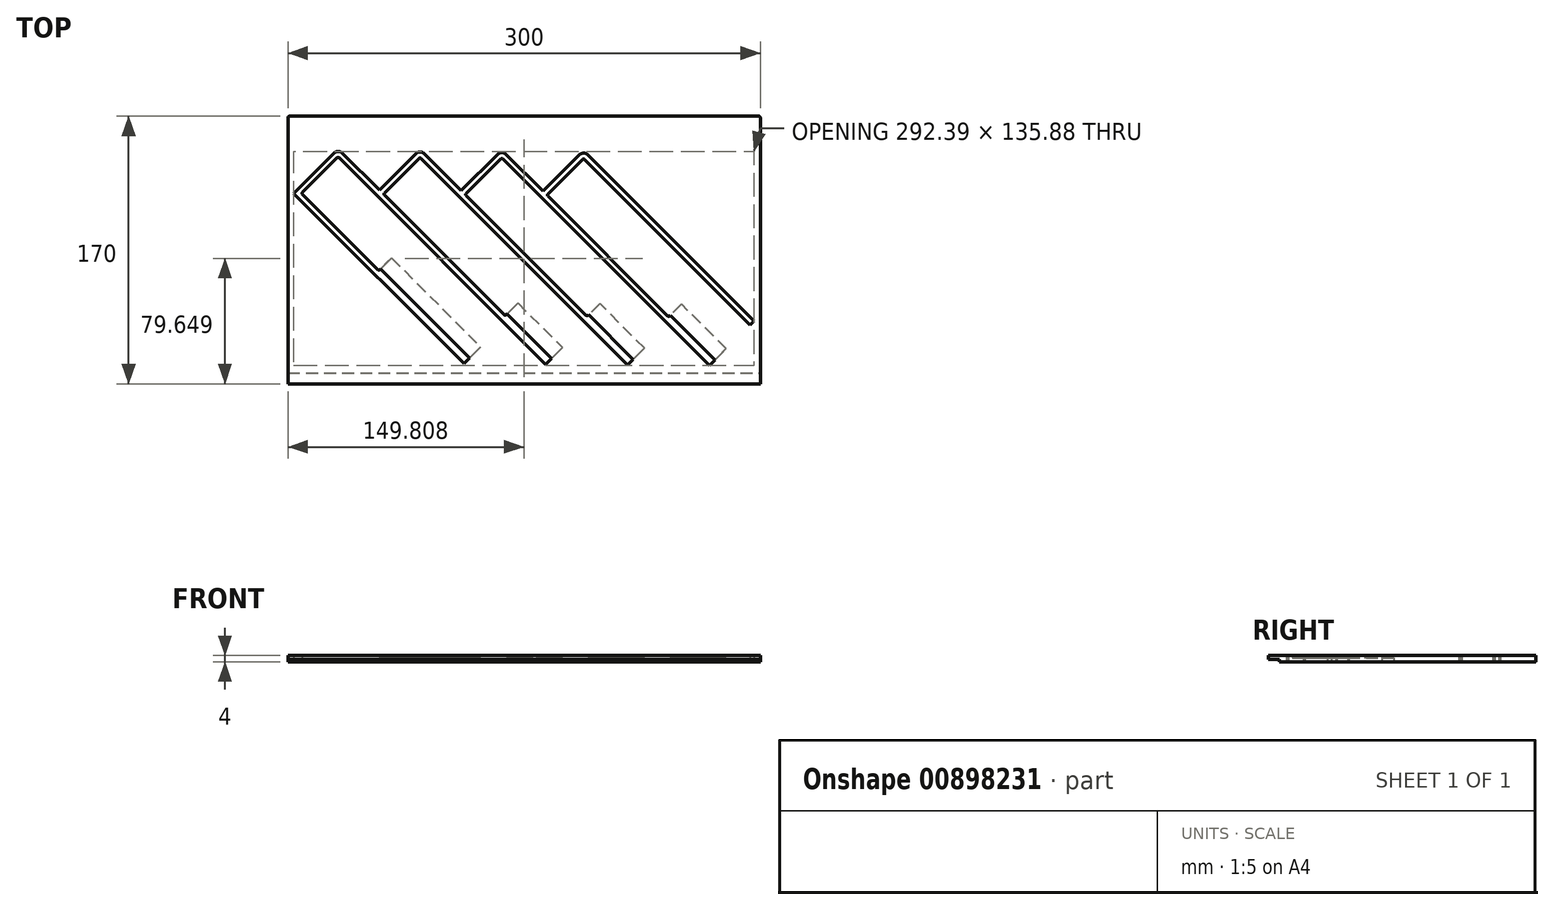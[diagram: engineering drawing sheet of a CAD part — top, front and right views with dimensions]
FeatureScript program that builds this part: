
annotation { "Feature Type Name" : "Feature", "Feature Type Description" : "" }
export const myFeature = defineFeature(function(context is Context, id is Id, definition is map)
    precondition{}
    {
        {
            var Q0;
            Q0=qCreatedBy(makeId("Top.planeOp"),FACE);
            var sketch = newSketch(context, id + "F0", { "sketchPlane" : qUnion([Q0])});
            skLineSegment(sketch, "E0.left", {"start": v(295.71, -89.91) * mm, "end": v(295.71, 79.09) * mm});
            skPoint(sketch, "E0.middle", {"position": v(0, 0) * mm});
            skLineSegment(sketch, "E1", {"start": v(186.35, 55.44) * mm, "end": v(291.71, -49.91) * mm});
            skLineSegment(sketch, "E2", {"start": v(291.71, -49.91) * mm, "end": v(289.24, -52.39) * mm});
            skLineSegment(sketch, "E3", {"start": v(263.43, -78.2) * mm, "end": v(155.24, 29.99) * mm});
            skLineSegment(sketch, "E4", {"start": v(157.72, 32.46) * mm, "end": v(180.7, 55.44) * mm});
            skLineSegment(sketch, "E5", {"start": v(236.91, -46.73) * mm, "end": v(160.9, 29.28) * mm});
            skLineSegment(sketch, "E6", {"start": v(160.9, 30.7) * mm, "end": v(182.82, 52.62) * mm});
            skLineSegment(sketch, "E7", {"start": v(184.23, 52.62) * mm, "end": v(289.24, -52.39) * mm});
            skLineSegment(sketch, "E8.trimOffspring", {"start": v(265.9, -75.72) * mm, "end": v(263.43, -78.2) * mm});
            skLineSegment(sketch, "E9", {"start": v(134.38, 55.8) * mm, "end": v(157.72, 32.46) * mm});
            skLineSegment(sketch, "E10", {"start": v(211.46, -77.84) * mm, "end": v(103.27, 30.34) * mm});
            skLineSegment(sketch, "E11", {"start": v(105.74, 32.82) * mm, "end": v(128.72, 55.8) * mm});
            skLineSegment(sketch, "E12", {"start": v(184.94, -46.38) * mm, "end": v(108.93, 29.64) * mm});
            skLineSegment(sketch, "E13", {"start": v(108.93, 31.05) * mm, "end": v(130.85, 52.97) * mm});
            skLineSegment(sketch, "E14", {"start": v(132.26, 52.97) * mm, "end": v(155.24, 29.99) * mm});
            skLineSegment(sketch, "E15.trimOffspring", {"start": v(213.93, -75.37) * mm, "end": v(211.46, -77.84) * mm});
            skLineSegment(sketch, "E16", {"start": v(82.4, 56.15) * mm, "end": v(105.74, 32.82) * mm});
            skLineSegment(sketch, "E17", {"start": v(159.48, -77.5) * mm, "end": v(51.3, 30.7) * mm});
            skLineSegment(sketch, "E18", {"start": v(53.77, 33.17) * mm, "end": v(76.75, 56.15) * mm});
            skLineSegment(sketch, "E19", {"start": v(132.97, -46.03) * mm, "end": v(56.95, 29.99) * mm});
            skLineSegment(sketch, "E20", {"start": v(56.95, 31.4) * mm, "end": v(78.87, 53.32) * mm});
            skLineSegment(sketch, "E21", {"start": v(80.29, 53.32) * mm, "end": v(103.27, 30.34) * mm});
            skLineSegment(sketch, "E22.trimOffspring", {"start": v(161.96, -75.02) * mm, "end": v(159.48, -77.5) * mm});
            skLineSegment(sketch, "E23", {"start": v(30.44, 56.5) * mm, "end": v(53.77, 33.17) * mm});
            skLineSegment(sketch, "E24", {"start": v(107.51, -77.14) * mm, "end": v(-0.68, 31.05) * mm});
            skLineSegment(sketch, "E25", {"start": v(-0.68, 31.05) * mm, "end": v(24.78, 56.5) * mm});
            skLineSegment(sketch, "E26", {"start": v(52.71, -17.39) * mm, "end": v(4.98, 30.34) * mm});
            skLineSegment(sketch, "E27", {"start": v(4.98, 31.76) * mm, "end": v(26.9, 53.68) * mm});
            skLineSegment(sketch, "E28", {"start": v(28.32, 53.68) * mm, "end": v(51.3, 30.7) * mm});
            skLineSegment(sketch, "E29.trimOffspring", {"start": v(109.99, -74.66) * mm, "end": v(107.51, -77.14) * mm});
            skLineSegment(sketch, "E30", {"start": v(-4.29, -89.91) * mm, "end": v(295.71, -89.91) * mm});
            skLineSegment(sketch, "E31", {"start": v(265.9, -75.72) * mm, "end": v(266.96, -74.66) * mm});
            skLineSegment(sketch, "E32", {"start": v(266.96, -74.66) * mm, "end": v(238.68, -46.38) * mm});
            skLineSegment(sketch, "E33", {"start": v(238.68, -46.38) * mm, "end": v(238.33, -46.73) * mm});
            skLineSegment(sketch, "E34", {"start": v(213.93, -75.37) * mm, "end": v(215, -74.3) * mm});
            skLineSegment(sketch, "E35", {"start": v(215, -74.3) * mm, "end": v(186.7, -46.03) * mm});
            skLineSegment(sketch, "E36", {"start": v(186.7, -46.03) * mm, "end": v(186.35, -46.38) * mm});
            skLineSegment(sketch, "E37", {"start": v(161.96, -75.02) * mm, "end": v(163.02, -73.96) * mm});
            skLineSegment(sketch, "E38", {"start": v(163.02, -73.96) * mm, "end": v(134.73, -45.67) * mm});
            skLineSegment(sketch, "E39", {"start": v(134.73, -45.67) * mm, "end": v(134.38, -46.03) * mm});
            skLineSegment(sketch, "E40", {"start": v(109.99, -74.66) * mm, "end": v(111.05, -73.6) * mm});
            skLineSegment(sketch, "E41", {"start": v(111.05, -73.6) * mm, "end": v(54.48, -17.03) * mm});
            skLineSegment(sketch, "E42", {"start": v(54.48, -17.03) * mm, "end": v(54.12, -17.39) * mm});
            skPoint(sketch, "E43.visualSharp", {"position": v(27.6, 59.33) * mm});
            skArc(sketch, "E43.filletArc", {"start": v(30.44, 56.5) * mm, "mid": v(27.6, 57.68) * mm, "end": v(24.78, 56.5) * mm});
            skPoint(sketch, "E44.visualSharp", {"position": v(79.58, 58.98) * mm});
            skArc(sketch, "E44.filletArc", {"start": v(82.4, 56.15) * mm, "mid": v(79.58, 57.32) * mm, "end": v(76.75, 56.15) * mm});
            skPoint(sketch, "E45.visualSharp", {"position": v(131.55, 58.63) * mm});
            skArc(sketch, "E45.filletArc", {"start": v(134.38, 55.8) * mm, "mid": v(131.55, 56.97) * mm, "end": v(128.72, 55.8) * mm});
            skPoint(sketch, "E46.visualSharp", {"position": v(183.53, 58.27) * mm});
            skArc(sketch, "E46.filletArc", {"start": v(186.35, 55.44) * mm, "mid": v(183.53, 56.62) * mm, "end": v(180.7, 55.44) * mm});
            skLineSegment(sketch, "E47", {"start": v(-4.29, 79.09) * mm, "end": v(-4.29, -89.91) * mm});
            skPoint(sketch, "E48.visualSharp", {"position": v(4.27, 31.05) * mm});
            skArc(sketch, "E48.filletArc", {"start": v(4.98, 31.76) * mm, "mid": v(4.69, 31.05) * mm, "end": v(4.98, 30.34) * mm});
            skPoint(sketch, "E49.visualSharp", {"position": v(56.25, 30.7) * mm});
            skArc(sketch, "E49.filletArc", {"start": v(56.95, 31.4) * mm, "mid": v(56.66, 30.7) * mm, "end": v(56.95, 29.99) * mm});
            skPoint(sketch, "E50.visualSharp", {"position": v(108.22, 30.34) * mm});
            skArc(sketch, "E50.filletArc", {"start": v(108.93, 31.05) * mm, "mid": v(108.63, 30.34) * mm, "end": v(108.93, 29.64) * mm});
            skPoint(sketch, "E51.visualSharp", {"position": v(160.2, 29.99) * mm});
            skArc(sketch, "E51.filletArc", {"start": v(160.9, 30.7) * mm, "mid": v(160.6, 29.99) * mm, "end": v(160.9, 29.28) * mm});
            skPoint(sketch, "E52.visualSharp", {"position": v(27.6, 54.38) * mm});
            skArc(sketch, "E52.filletArc", {"start": v(28.32, 53.68) * mm, "mid": v(27.6, 53.97) * mm, "end": v(26.9, 53.68) * mm});
            skPoint(sketch, "E53.visualSharp", {"position": v(79.58, 54.03) * mm});
            skArc(sketch, "E53.filletArc", {"start": v(80.29, 53.32) * mm, "mid": v(79.58, 53.62) * mm, "end": v(78.87, 53.32) * mm});
            skPoint(sketch, "E54.visualSharp", {"position": v(131.55, 53.68) * mm});
            skArc(sketch, "E54.filletArc", {"start": v(132.26, 52.97) * mm, "mid": v(131.55, 53.26) * mm, "end": v(130.85, 52.97) * mm});
            skPoint(sketch, "E55.visualSharp", {"position": v(183.53, 53.32) * mm});
            skArc(sketch, "E55.filletArc", {"start": v(184.23, 52.62) * mm, "mid": v(183.53, 52.9) * mm, "end": v(182.82, 52.62) * mm});
            skLineSegment(sketch, "E56", {"start": v(-3.29, 80.09) * mm, "end": v(294.71, 80.09) * mm});
            skPoint(sketch, "E57.visualSharp", {"position": v(-4.29, 80.09) * mm});
            skArc(sketch, "E57.filletArc", {"start": v(-3.29, 80.09) * mm, "mid": v(-4, 79.8) * mm, "end": v(-4.29, 79.09) * mm});
            skPoint(sketch, "E58.visualSharp", {"position": v(295.71, 80.09) * mm});
            skArc(sketch, "E58.filletArc", {"start": v(295.71, 79.09) * mm, "mid": v(295.42, 79.8) * mm, "end": v(294.71, 80.09) * mm});
            skPoint(sketch, "E59.visualSharp", {"position": v(53.42, -18.1) * mm});
            skArc(sketch, "E59.filletArc", {"start": v(52.71, -17.39) * mm, "mid": v(53.42, -17.68) * mm, "end": v(54.12, -17.39) * mm});
            skPoint(sketch, "E60.visualSharp", {"position": v(133.67, -46.73) * mm});
            skArc(sketch, "E60.filletArc", {"start": v(132.97, -46.03) * mm, "mid": v(133.67, -46.32) * mm, "end": v(134.38, -46.03) * mm});
            skPoint(sketch, "E61.visualSharp", {"position": v(185.65, -47.09) * mm});
            skArc(sketch, "E61.filletArc", {"start": v(184.94, -46.38) * mm, "mid": v(185.65, -46.67) * mm, "end": v(186.35, -46.38) * mm});
            skPoint(sketch, "E62.visualSharp", {"position": v(237.62, -47.44) * mm});
            skArc(sketch, "E62.filletArc", {"start": v(236.91, -46.73) * mm, "mid": v(237.62, -47.03) * mm, "end": v(238.33, -46.73) * mm});
            skSolve(sketch);
        }
        {
            var Q0;
            Q0=qSketchRegion(id+"F0",true);
            extrude(context, id + "F1", {"entities" : qUnion([Q0]), "depth" : 4 * mm});
        }
        {
            var Q0;
            Q0=makeQuery(id+"F1.opExtrude","CAP_FACE",FACE,{"disambiguationData":[OSD([sQuery(id+"F0.wireOp",EDGE,"E0.top"),sQuery(id+"F0.wireOp",EDGE,"E0.left"),sQuery(id+"F0.wireOp",EDGE,"E0.right"),sQuery(id+"F0.wireOp",EDGE,"E1"),sQuery(id+"F0.wireOp",EDGE,"E2"),sQuery(id+"F0.wireOp",EDGE,"E3"),sQuery(id+"F0.wireOp",EDGE,"E4"),sQuery(id+"F0.wireOp",EDGE,"E5"),sQuery(id+"F0.wireOp",EDGE,"E6"),sQuery(id+"F0.wireOp",EDGE,"E7"),sQuery(id+"F0.wireOp",EDGE,"E8.trimOffspring"),sQuery(id+"F0.wireOp",EDGE,"E9"),sQuery(id+"F0.wireOp",EDGE,"E10"),sQuery(id+"F0.wireOp",EDGE,"E11"),sQuery(id+"F0.wireOp",EDGE,"E12"),sQuery(id+"F0.wireOp",EDGE,"E13"),sQuery(id+"F0.wireOp",EDGE,"E14"),sQuery(id+"F0.wireOp",EDGE,"E15.trimOffspring"),sQuery(id+"F0.wireOp",EDGE,"E16"),sQuery(id+"F0.wireOp",EDGE,"E17"),sQuery(id+"F0.wireOp",EDGE,"E18"),sQuery(id+"F0.wireOp",EDGE,"E19"),sQuery(id+"F0.wireOp",EDGE,"E20"),sQuery(id+"F0.wireOp",EDGE,"E21"),sQuery(id+"F0.wireOp",EDGE,"E22.trimOffspring"),sQuery(id+"F0.wireOp",EDGE,"E23"),sQuery(id+"F0.wireOp",EDGE,"E24"),sQuery(id+"F0.wireOp",EDGE,"E25"),sQuery(id+"F0.wireOp",EDGE,"E26"),sQuery(id+"F0.wireOp",EDGE,"E27"),sQuery(id+"F0.wireOp",EDGE,"E28"),sQuery(id+"F0.wireOp",EDGE,"E29.trimOffspring"),sQuery(id+"F0.wireOp",EDGE,"GlQ2Ejkr-JzWv-SczF-AkSn-IIUsIDUsQLDF"),sQuery(id+"F0.wireOp",EDGE,"4rRTUtHd-6Czx-Y02v-wLBt-rsdX1xkabp84"),sQuery(id+"F0.wireOp",EDGE,"4G5GyRjq-5n8M-YiYg-MP7m-sspNvvtmjU4K"),sQuery(id+"F0.wireOp",EDGE,"ICIfgb8K-1rxL-Ru2O-Csyg-Pg72DHdsQuOJ"),sQuery(id+"F0.wireOp",EDGE,"E30"),sQuery(id+"F0.wireOp",EDGE,"8IGRu6me-QNIK-KxZd-YoE2-obK5ITrom9I0"),sQuery(id+"F0.wireOp",EDGE,"ET2SPLNs-E16K-yzbb-k3nE-j9QhBZggRVGa"),sQuery(id+"F0.wireOp",EDGE,"ztZXadrO-MKuG-NGwv-NWga-JcB19pq0CV4f"),sQuery(id+"F0.wireOp",EDGE,"rMW3URec-0C8R-i97H-GSKa-9mzG0eoT4OPy"),sQuery(id+"F0.wireOp",EDGE,"l2nM3VSt-hcp3-IfvZ-Vc9z-1xBHJXzoDHYJ"),sQuery(id+"F0.wireOp",EDGE,"7f4JG1PR-e8fq-IrSw-QAHP-AJHShleLprlO"),sQuery(id+"F0.wireOp",EDGE,"S5SOpvzM-2vfI-Hdyw-8EQE-COdiVjVuYll8"),sQuery(id+"F0.wireOp",EDGE,"2IVgYnUZ-HQwh-ZoWA-2HmY-ZoItcJW675aA"),sQuery(id+"F0.wireOp",EDGE,"WKOqhnvw-Yy6J-5Mtj-p5Rz-aYmJGyGwGpHv"),sQuery(id+"F0.wireOp",EDGE,"Wq4ZA5YM-xzJ0-yVii-3j4H-AYTGBk09bdcb"),sQuery(id+"F0.wireOp",EDGE,"0u9dqrDR-6jrO-UaEj-ZAFe-c7Mw1oq4VQrV"),sQuery(id+"F0.wireOp",EDGE,"gIA7jmsT-nlDV-00d0-acZ5-NCJ1QFAXyANS")])],"isStart":true});
            var sketch = newSketch(context, id + "F2", { "sketchPlane" : qUnion([Q0])});
            skLineSegment(sketch, "E63", {"start": v(266.96, 74.66) * mm, "end": v(274.03, 67.6) * mm});
            skLineSegment(sketch, "E64", {"start": v(274.03, 67.6) * mm, "end": v(245.75, 39.3) * mm});
            skLineSegment(sketch, "E65", {"start": v(245.75, 39.3) * mm, "end": v(238.68, 46.38) * mm});
            skLineSegment(sketch, "E66", {"start": v(215, 74.3) * mm, "end": v(222.06, 67.24) * mm});
            skLineSegment(sketch, "E67", {"start": v(222.06, 67.24) * mm, "end": v(193.78, 38.95) * mm});
            skLineSegment(sketch, "E68", {"start": v(193.78, 38.95) * mm, "end": v(186.7, 46.03) * mm});
            skLineSegment(sketch, "E69", {"start": v(266.96, 74.66) * mm, "end": v(238.68, 46.38) * mm});
            skLineSegment(sketch, "E70", {"start": v(215, 74.3) * mm, "end": v(186.7, 46.03) * mm});
            skLineSegment(sketch, "E71", {"start": v(163.02, 73.96) * mm, "end": v(134.73, 45.67) * mm});
            skLineSegment(sketch, "E72", {"start": v(134.73, 45.67) * mm, "end": v(141.8, 38.6) * mm});
            skLineSegment(sketch, "E73", {"start": v(141.8, 38.6) * mm, "end": v(170.09, 66.88) * mm});
            skLineSegment(sketch, "E74", {"start": v(170.09, 66.88) * mm, "end": v(163.02, 73.96) * mm});
            skLineSegment(sketch, "E75", {"start": v(111.05, 73.6) * mm, "end": v(54.48, 17.03) * mm});
            skLineSegment(sketch, "E76", {"start": v(54.48, 17.03) * mm, "end": v(61.55, 9.96) * mm});
            skLineSegment(sketch, "E77", {"start": v(61.55, 9.96) * mm, "end": v(118.12, 66.53) * mm});
            skLineSegment(sketch, "E78", {"start": v(118.12, 66.53) * mm, "end": v(111.05, 73.6) * mm});
            skLineSegment(sketch, "E79", {"start": v(-4.29, 82.91) * mm, "end": v(295.71, 82.91) * mm});
            skLineSegment(sketch, "E80", {"start": v(295.71, 82.91) * mm, "end": v(295.71, 89.91) * mm});
            skLineSegment(sketch, "E81", {"start": v(295.71, 89.91) * mm, "end": v(-4.29, 89.91) * mm});
            skLineSegment(sketch, "E82", {"start": v(-4.29, 89.91) * mm, "end": v(-4.29, 82.91) * mm});
            skSolve(sketch);
        }
        {
            var Q0;
            Q0=makeQuery(id+"F2.imprint","IMPRINT",FACE,{"disambiguationData":[TD([[makeQuery(id+"F2.imprint","IMPRINT",EDGE,{"derivedFrom":sQuery(id+"F2.wireOp",EDGE,"E79")}),1.0]])]});
            extrude(context, id + "F3", {"entities" : qUnion([Q0]), "operationType" : NewBodyOperationType.REMOVE, "oppositeDirection" : true, "depth" : 1.5 * mm});
        }
        {
            var Q0;
            Q0=makeQuery(id+"F2.imprint","IMPRINT",FACE,{"disambiguationData":[TD([[makeQuery(id+"F2.imprint","IMPRINT",EDGE,{"derivedFrom":sQuery(id+"F2.wireOp",EDGE,"E75")}),1.0]])]});
            var Q1;
            Q1=makeQuery(id+"F2.imprint","IMPRINT",FACE,{"disambiguationData":[TD([[makeQuery(id+"F2.imprint","IMPRINT",EDGE,{"derivedFrom":sQuery(id+"F2.wireOp",EDGE,"E71")}),1.0]])]});
            var Q2;
            Q2=makeQuery(id+"F2.imprint","IMPRINT",FACE,{"disambiguationData":[TD([[makeQuery(id+"F2.imprint","IMPRINT",EDGE,{"derivedFrom":sQuery(id+"F2.wireOp",EDGE,"E66")}),-1.0]])]});
            var Q3;
            Q3=makeQuery(id+"F2.imprint","IMPRINT",FACE,{"disambiguationData":[TD([[makeQuery(id+"F2.imprint","IMPRINT",EDGE,{"derivedFrom":sQuery(id+"F2.wireOp",EDGE,"E63")}),-1.0]])]});
            extrude(context, id + "F4", {"entities" : qUnion([Q0, Q1, Q2, Q3]), "operationType" : NewBodyOperationType.REMOVE, "oppositeDirection" : true, "depth" : 2.5 * mm});
        }
    });
